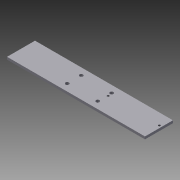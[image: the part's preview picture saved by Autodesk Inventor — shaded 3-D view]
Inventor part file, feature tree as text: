
AUTODESK INVENTOR PART (.ipt)
format: ipt  version: 2012 (Build 160160000, 160)  size: 114,688 bytes
history: native  units: mm
features: sketch x3, hole x2, reference x2, extrude x1
ambient origin geometry x8: Origin, YZ Plane, XZ Plane, XY Plane, X Axis, Y Axis, Z Axis, Center Point
bodies: Solid1 (feature_tree)
feature tree (8):
  extrude  "Extrusion1"  Depth=35.56mm
  hole  "Hole5"  [1 undecoded]
  hole  "Hole6"  [1 undecoded]
  sketch  "Sketch1"  dims[d0=175.26mm d1=35.56mm]
  sketch  "Sketch7"  dims[d2=3.175mm d3=0.0mm d97=26.67mm]
  sketch  "Sketch8"  dims[d98=8.89mm d99=8.89mm d100=26.67mm d101=8.89mm d102=4.4958mm d103=19.05mm d104=12.7mm d105=2.794mm d106=14.3117mm d107=25.4mm d108=20.594885mm d109=2.6416mm d110=19.05mm d111=9.525mm d112=6.35mm d113=14.3117mm d114=25.4mm d115=20.594885mm]
  reference  "Reference3"
  reference  "Reference4"
note: 2 required parameter values undecoded (feature->parameter linkage not recoverable at this tier; creation-order binding heuristic only, values carry confidence <= 0.55)
